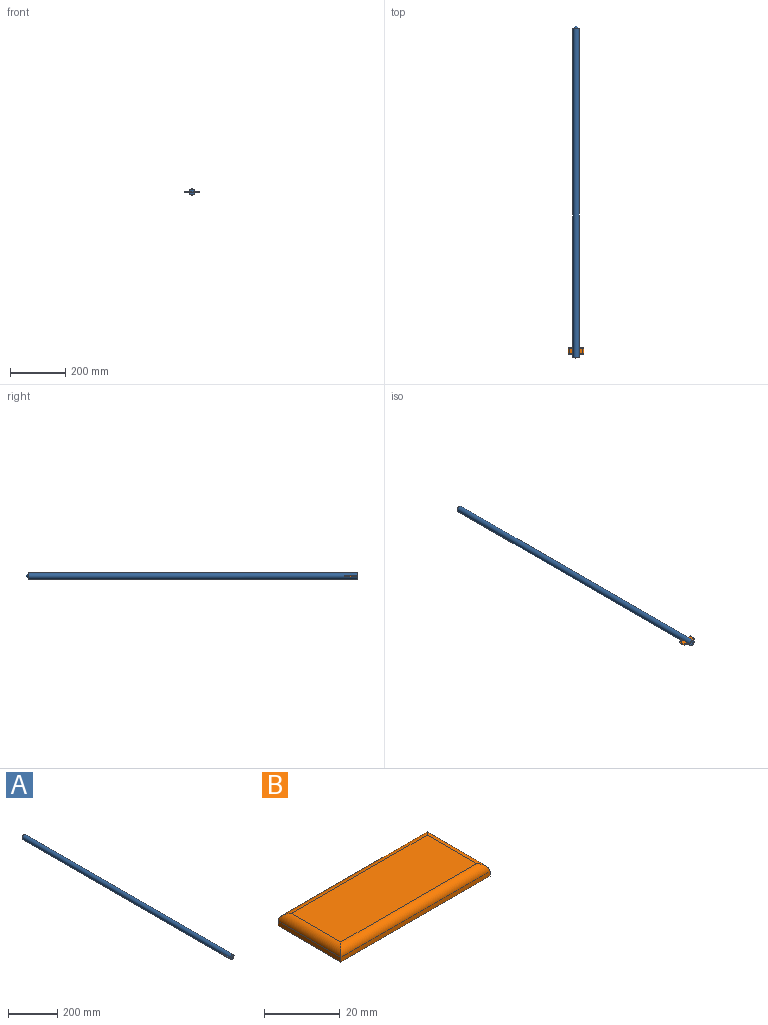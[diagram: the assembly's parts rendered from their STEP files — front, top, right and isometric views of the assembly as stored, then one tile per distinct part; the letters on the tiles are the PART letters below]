
ASSEMBLY  parts=2 mates=1
PART A: 8 faces, bbox 22x1200x22 mm
  f0: plane 21.77x9.46mm, normal (0,-1,0), area 155.5mm2, adj f1,f5
  f1: cylinder r=11mm len=1190mm, axis (0,1,0), area 81825.9mm2, adj f0,f2,f4,f5,f6,f7
  f2: plane 21.38x8.4mm, normal (0,-1,0), area 133.4mm2, adj f1,f6
  f3: plane 2x2mm, normal (0,1,0), area 3.1mm2, adj f7
  f4: plane 22x4.22mm, normal (0,-1,0), area 91.3mm2, adj f1,f5,f6
  f5: plane 50x21.77mm, normal (0,0,-1), area 1088.6mm2, adj f0,f1,f4
  f6: plane 50x21.38mm, normal (0,0,1), area 1068.8mm2, adj f1,f2,f4
  f7: cone r=11mm half-angle=45deg, axis (0,-1,0), area 533.1mm2, adj f1,f3
PART B: 10 faces, bbox 55.6x23.4x4 mm
  f0: plane 23.45x1.5mm, normal (-1,0,0), area 35.2mm2, adj f1,f3,f5,f6
  f1: plane 55.56x1.5mm, normal (0,-1,0), area 83.3mm2, adj f0,f2,f5,f7
  f2: plane 23.45x1.5mm, normal (1,0,0), area 35.2mm2, adj f1,f3,f5,f9
  f3: plane 55.56x1.5mm, normal (0,1,0), area 83.3mm2, adj f0,f2,f5,f8
  f4: plane 50.56x18.45mm, normal (0,0,1), area 932.8mm2, adj f6,f7,f8,f9
  f5: plane 55.56x23.45mm, normal (0,0,-1), area 1302.8mm2, adj f0,f1,f2,f3
  f6: cylinder r=2.5mm len=23.45mm, axis (0,1,0), area 84.9mm2, adj f0,f4,f7,f8
  f7: cylinder r=2.5mm len=55.56mm, axis (-1,0,0), area 211.1mm2, adj f1,f4,f6,f9
  f8: cylinder r=2.5mm len=55.56mm, axis (1,0,0), area 211.1mm2, adj f3,f4,f6,f9
  f9: cylinder r=2.5mm len=23.45mm, axis (0,-1,0), area 84.9mm2, adj f2,f4,f7,f8
PLACE A t=(-197.3,1.81,-166.2)mm
PLACE B rot(axis=(0,-1,0),0.2deg) t=(-201.28,-1174.5,-167.89)mm
MATE fastened B.f4 <-> A.f5  axis (0,0,1) through (-197.5,-1173.19,-163.87)mm
